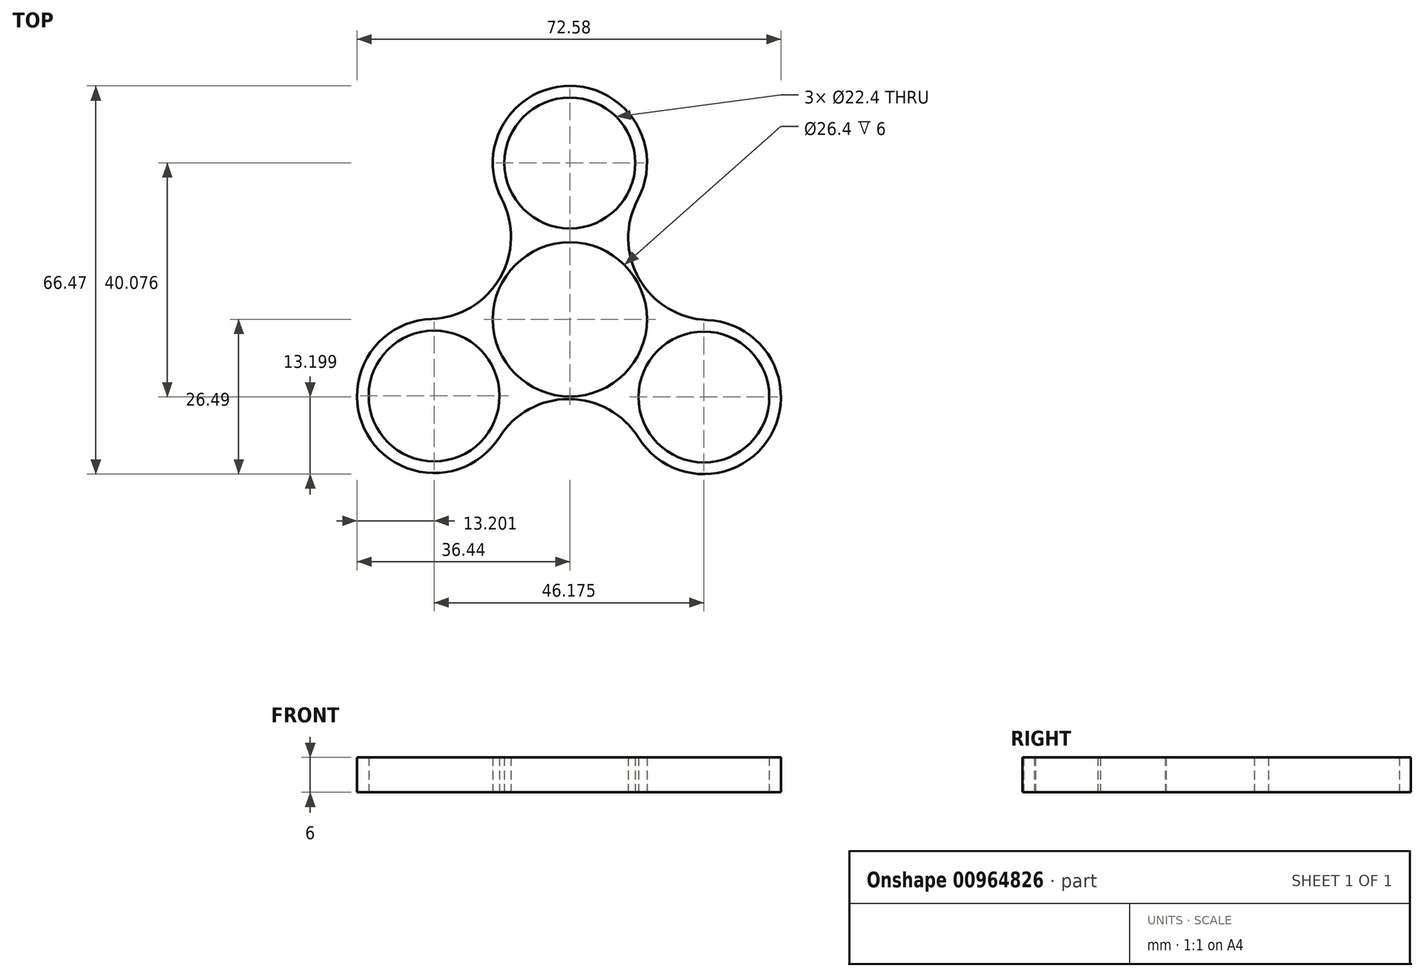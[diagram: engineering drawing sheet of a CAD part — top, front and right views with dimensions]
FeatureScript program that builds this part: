
annotation { "Feature Type Name" : "Feature", "Feature Type Description" : "" }
export const myFeature = defineFeature(function(context is Context, id is Id, definition is map)
    precondition{}
    {
        {
            var Q0;
            Q0=qCreatedBy(makeId("Top.planeOp"),FACE);
            var sketch = newSketch(context, id + "F0", { "sketchPlane" : qUnion([Q0])});
            skCircle(sketch, "E0", {"center": v(0, 0) * mm, "radius": 11.2 * mm});
            skCircle(sketch, "E1", {"center": v(0, 0) * mm, "radius": 13.2 * mm});
            skCircle(sketch, "E2", {"center": v(0, 26.78) * mm, "radius": 11.2 * mm});
            skCircle(sketch, "E3", {"center": v(0, 26.78) * mm, "radius": 13.2 * mm});
            skCircle(sketch, "E4.1.0", {"center": v(-23.24, -13.12) * mm, "radius": 13.2 * mm});
            skCircle(sketch, "E4.1.1", {"center": v(-23.24, -13.12) * mm, "radius": 11.2 * mm});
            skCircle(sketch, "E4.2.0", {"center": v(22.94, -13.3) * mm, "radius": 13.2 * mm});
            skCircle(sketch, "E4.2.1", {"center": v(22.94, -13.3) * mm, "radius": 11.2 * mm});
            skPoint(sketch, "E4.center", {"position": v(-0.1, 0.13) * mm});
            skArc(sketch, "E5", {"start": v(11.64, 20.57) * mm, "mid": v(11.85, 6.96) * mm, "end": v(23.48, -0.1) * mm});
            skArc(sketch, "E6.1.0", {"start": v(-23.68, 0.08) * mm, "mid": v(-12, 7.05) * mm, "end": v(-11.7, 20.66) * mm});
            skArc(sketch, "E6.2.0", {"start": v(11.73, -20.27) * mm, "mid": v(-0.15, -13.64) * mm, "end": v(-12.09, -20.18) * mm});
            skSolve(sketch);
        }
        {
            var Q0;
            Q0 = qSketchRegion(id + "F0", true);
            extrude(context, id + "F1", {"entities" : qUnion([Q0]), "depth" : 6 * mm, "offsetDistance" : 25 * mm});
        }
    });
